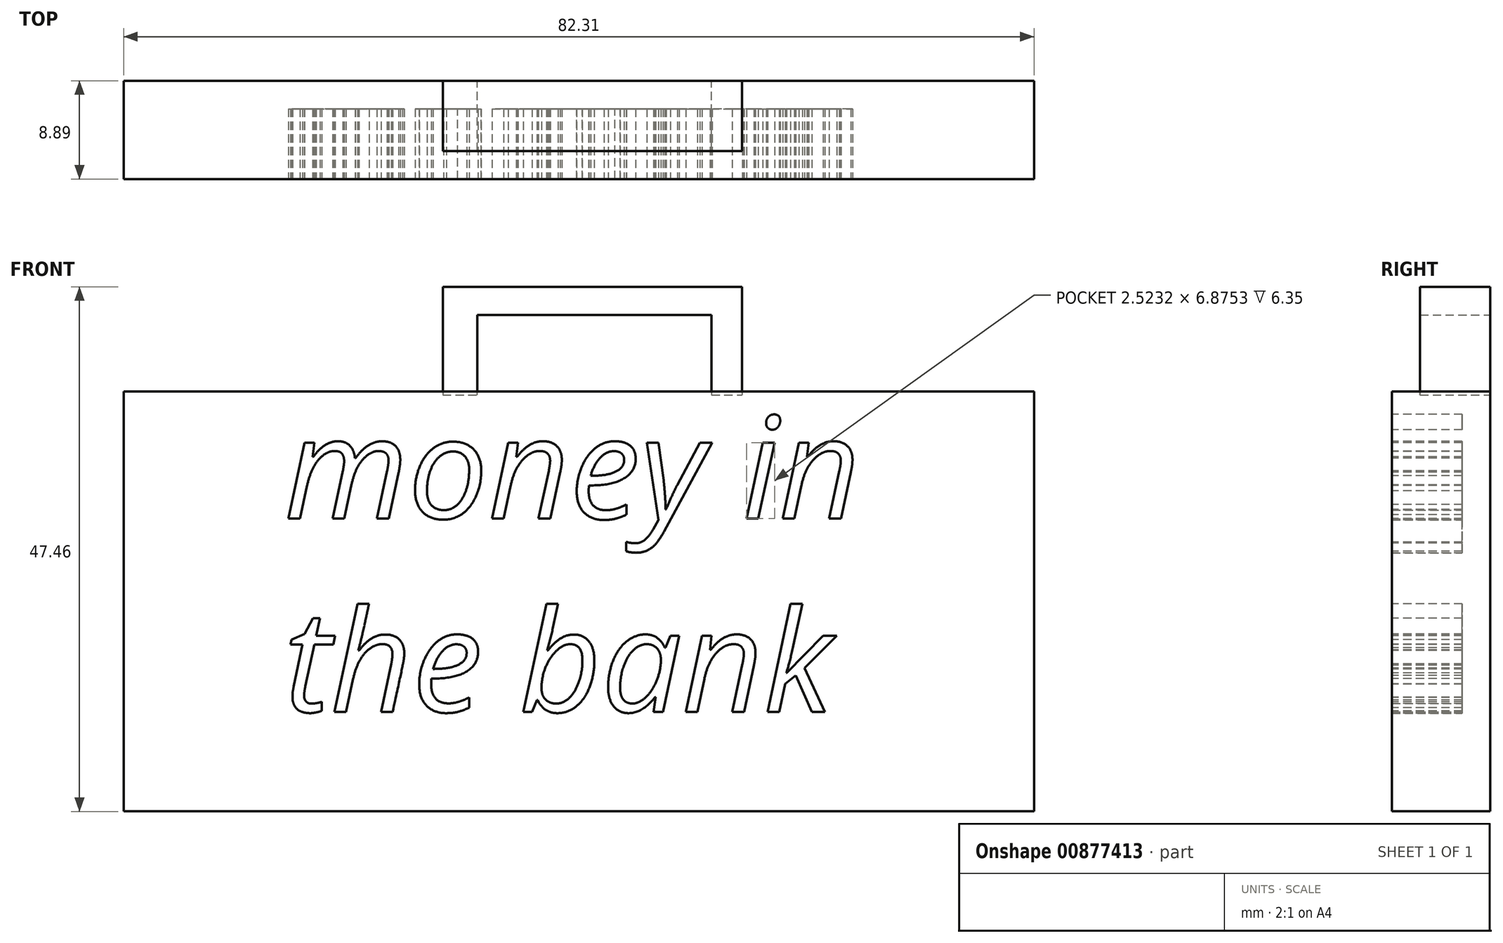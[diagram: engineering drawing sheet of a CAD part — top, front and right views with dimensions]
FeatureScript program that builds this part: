
annotation { "Feature Type Name" : "Feature", "Feature Type Description" : "" }
export const myFeature = defineFeature(function(context is Context, id is Id, definition is map)
    precondition{}
    {
        {
            var Q0;
            Q0=qCreatedBy(makeId("Front.planeOp"),FACE);
            var sketch = newSketch(context, id + "F0", { "sketchPlane" : qUnion([Q0])});
            skLineSegment(sketch, "E0.bottom", {"start": v(-46.77, 26.33) * mm, "end": v(35.54, 26.33) * mm});
            skLineSegment(sketch, "E0.top", {"start": v(-46.77, -11.66) * mm, "end": v(35.54, -11.66) * mm});
            skLineSegment(sketch, "E0.left", {"start": v(-46.77, 26.33) * mm, "end": v(-46.77, -11.66) * mm});
            skLineSegment(sketch, "E0.right", {"start": v(35.54, 26.33) * mm, "end": v(35.54, -11.66) * mm});
            skSolve(sketch);
        }
        {
            var Q0;
            Q0 = qSketchRegion(id + "F0", true);
            extrude(context, id + "F1", {"entities" : qUnion([Q0]), "depth" : 8.9 * mm, "offsetDistance" : 25.4 * mm});
        }
        {
            var Q0;
            Q0=qCreatedBy(makeId("Front.planeOp"),FACE);
            var sketch = newSketch(context, id + "F2", { "sketchPlane" : qUnion([Q0])});
            skLineSegment(sketch, "E1.bottom", {"start": v(-17.92, 35.8) * mm, "end": v(9.13, 35.8) * mm});
            skLineSegment(sketch, "E1.top", {"start": v(-17.92, 26.01) * mm, "end": v(-14.78, 26.01) * mm});
            skLineSegment(sketch, "E1.left", {"start": v(-17.92, 35.8) * mm, "end": v(-17.92, 26.01) * mm});
            skLineSegment(sketch, "E1.right", {"start": v(9.13, 35.8) * mm, "end": v(9.13, 26.01) * mm});
            skLineSegment(sketch, "E2", {"start": v(-14.78, 26.01) * mm, "end": v(-14.78, 33.25) * mm});
            skLineSegment(sketch, "E3", {"start": v(-14.78, 33.25) * mm, "end": v(6.38, 33.25) * mm});
            skLineSegment(sketch, "E4", {"start": v(6.38, 33.25) * mm, "end": v(6.38, 26.01) * mm});
            skLineSegment(sketch, "E5.trimOffspring", {"start": v(6.38, 26.01) * mm, "end": v(9.13, 26.01) * mm});
            skSolve(sketch);
        }
        {
            var Q0;
            Q0=makeQuery(id+"F2.imprint","IMPRINT",FACE,{"disambiguationData":[TD([[makeQuery(id+"F2.imprint","IMPRINT",EDGE,{"derivedFrom":sQuery(id+"F2.wireOp",EDGE,"E1.bottom")}),-1.0]])]});
            var Q1;
            Q1=sQuery(id+"F2.wireOp",EDGE,"E1.left");
            var Q2;
            Q2=sQuery(id+"F2.wireOp",EDGE,"E1.right");
            var Q3;
            Q3=sQuery(id+"F2.wireOp",EDGE,"E1.bottom");
            extrude(context, id + "F3", {"entities" : qUnion([Q0]), "surfaceEntities" : qUnion([Q1, Q2, Q3]), "depth" : 6.35 * mm, "offsetDistance" : 25.4 * mm});
        }
        {
            var Q0;
            Q0=makeQuery(id+"F1.opExtrude","CAP_FACE",FACE,{"disambiguationData":[OSD([sQuery(id+"F0.wireOp",EDGE,"E0.bottom"),sQuery(id+"F0.wireOp",EDGE,"E0.top"),sQuery(id+"F0.wireOp",EDGE,"E0.left"),sQuery(id+"F0.wireOp",EDGE,"E0.right")])],"isStart":false});
            var sketch = newSketch(context, id + "F4", { "sketchPlane" : qUnion([Q0])});
            skSolve(sketch);
        }
        {
            var Q0;
            Q0=makeQuery(id+"F4.imprint","IMPRINT",FACE,{"disambiguationData":[TD([[makeQuery(id+"F4.imprint","IMPRINT",EDGE,{"derivedFrom":makeQuery(id+"F1.opExtrude","CAP_EDGE",EDGE,{"disambiguationData":[OSD([sQuery(id+"F0.wireOp",EDGE,"E0.bottom")])],"isStart":false})}),-1.0]])]});
            var sketch = newSketch(context, id + "F5", { "sketchPlane" : qUnion([Q0])});
            skText(sketch, "E6", { "text": "money in\nthe bank\n", "fontName": "OpenSans-Italic.ttf"});
            const initialGuessF5  = {"E6": [-0.03225, 0.01483, 1, 0, 0.00925]};
            skSetInitialGuess(sketch, initialGuessF5);
            skSolve(sketch);
        }
        {
            var Q0;
            Q0 = qSketchRegion(id + "F5", true);
            extrude(context, id + "F6", {"entities" : qUnion([Q0]), "operationType" : NewBodyOperationType.REMOVE, "oppositeDirection" : true, "depth" : 6.35 * mm, "offsetDistance" : 25.4 * mm});
        }
    });
